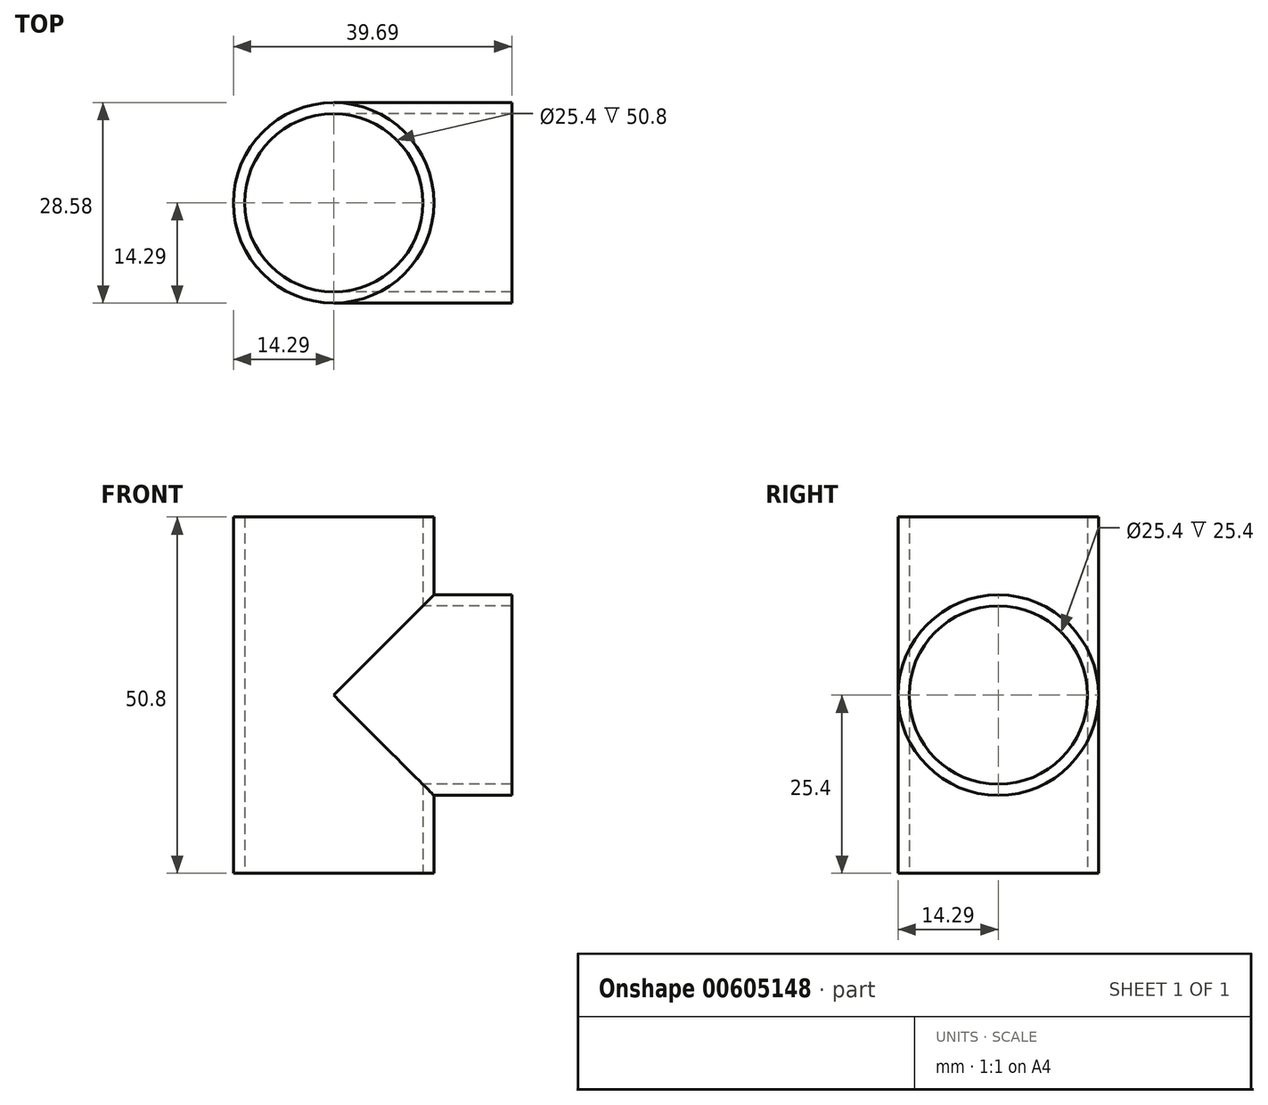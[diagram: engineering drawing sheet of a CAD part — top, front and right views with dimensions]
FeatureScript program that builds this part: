
annotation { "Feature Type Name" : "Feature", "Feature Type Description" : "" }
export const myFeature = defineFeature(function(context is Context, id is Id, definition is map)
    precondition{}
    {
        {
            var Q0;
            Q0=qCreatedBy(makeId("Top.planeOp"),FACE);
            var sketch = newSketch(context, id + "F0", { "sketchPlane" : qUnion([Q0])});
            skLineSegment(sketch, "E0", {"start": v(0, 0) * mm, "end": v(12.7, 0) * mm});
            skCircle(sketch, "E1", {"center": v(0, 0) * mm, "radius": 12.7 * mm});
            skCircle(sketch, "E2.0", {"center": v(0, 0) * mm, "radius": 14.29 * mm});
            skSolve(sketch);
        }
        {
            var Q0;
            Q0=qCreatedBy(makeId("Top.planeOp"),FACE);
            var sketch = newSketch(context, id + "F1", { "sketchPlane" : qUnion([Q0])});
            skSolve(sketch);
        }
        {
            var Q0;
            Q0=qSketchRegion(id+"F1",true);
            var Q1;
            Q1=makeQuery(id+"F0.imprint","IMPRINT",FACE,{"disambiguationData":[TD([[makeQuery(id+"F0.imprint","IMPRINT",EDGE,{"derivedFrom":sQuery(id+"F0.wireOp",EDGE,"E1")}),-1.0]])]});
            extrude(context, id + "F2", {"entities" : qUnion([Q0, Q1]), "depth" : 25.4 * mm, "offsetDistance" : 25.4 * mm, "hasSecondDirection" : true, "secondDirectionOppositeDirection" : true, "secondDirectionDepth" : 25.4 * mm});
        }
        {
            var Q0;
            Q0=qCreatedBy(makeId("Right.planeOp"),FACE);
            var sketch = newSketch(context, id + "F3", { "sketchPlane" : qUnion([Q0])});
            skCircle(sketch, "E3", {"center": v(0, 0) * mm, "radius": 14.29 * mm});
            skCircle(sketch, "E4.0", {"center": v(0, 0) * mm, "radius": 12.7 * mm});
            skSolve(sketch);
        }
        {
            var Q0;
            Q0 = qSketchRegion(id + "F3", true);
            extrude(context, id + "F4", {"entities" : qUnion([Q0]), "operationType" : NewBodyOperationType.ADD, "depth" : 25.4 * mm, "offsetDistance" : 25.4 * mm});
        }
        {
            var Q0;
            Q0=makeQuery(id+"F4.opExtrude","CAP_FACE",FACE,{"disambiguationData":[OSD([sQuery(id+"F3.wireOp",EDGE,"E3"),sQuery(id+"F3.wireOp",EDGE,"E4.0")])],"isStart":false});
            var sketch = newSketch(context, id + "F5", { "sketchPlane" : qUnion([Q0])});
            skSolve(sketch);
        }
        {
            var Q0;
            Q0 = qSketchRegion(id + "F5", true);
            var Q1;
            Q1=makeQuery(id+"F5.imprint","IMPRINT",FACE,{"disambiguationData":[TD([[makeQuery(id+"F5.imprint","IMPRINT",EDGE,{"derivedFrom":makeQuery(id+"F4.opExtrude","CAP_EDGE",EDGE,{"disambiguationData":[OSD([sQuery(id+"F3.wireOp",EDGE,"E4.0")])],"isStart":false})}),1.0]])]});
            extrude(context, id + "F6", {"entities" : qUnion([Q0, Q1]), "operationType" : NewBodyOperationType.REMOVE, "oppositeDirection" : true, "depth" : 25.4 * mm, "offsetDistance" : 25.4 * mm});
        }
        {
            var Q0;
            Q0=makeQuery(id+"F2.opExtrude","CAP_FACE",FACE,{"disambiguationData":[OSD([sQuery(id+"F0.wireOp",EDGE,"E1"),sQuery(id+"F0.wireOp",EDGE,"E2.0")])],"isStart":true});
            var sketch = newSketch(context, id + "F7", { "sketchPlane" : qUnion([Q0])});
            skSolve(sketch);
        }
        {
            var Q0;
            Q0 = qSketchRegion(id + "F7", true);
            var Q1;
            Q1=makeQuery(id+"F7.imprint","IMPRINT",FACE,{"disambiguationData":[TD([[makeQuery(id+"F7.imprint","IMPRINT",EDGE,{"derivedFrom":makeQuery(id+"F2.opExtrude","CAP_EDGE",EDGE,{"disambiguationData":[OSD([sQuery(id+"F0.wireOp",EDGE,"E1")])],"isStart":true})}),-1.0]])]});
            extrude(context, id + "F8", {"entities" : qUnion([Q0, Q1]), "operationType" : NewBodyOperationType.REMOVE, "oppositeDirection" : true, "depth" : 50.8 * mm, "offsetDistance" : 25.4 * mm});
        }
    });
